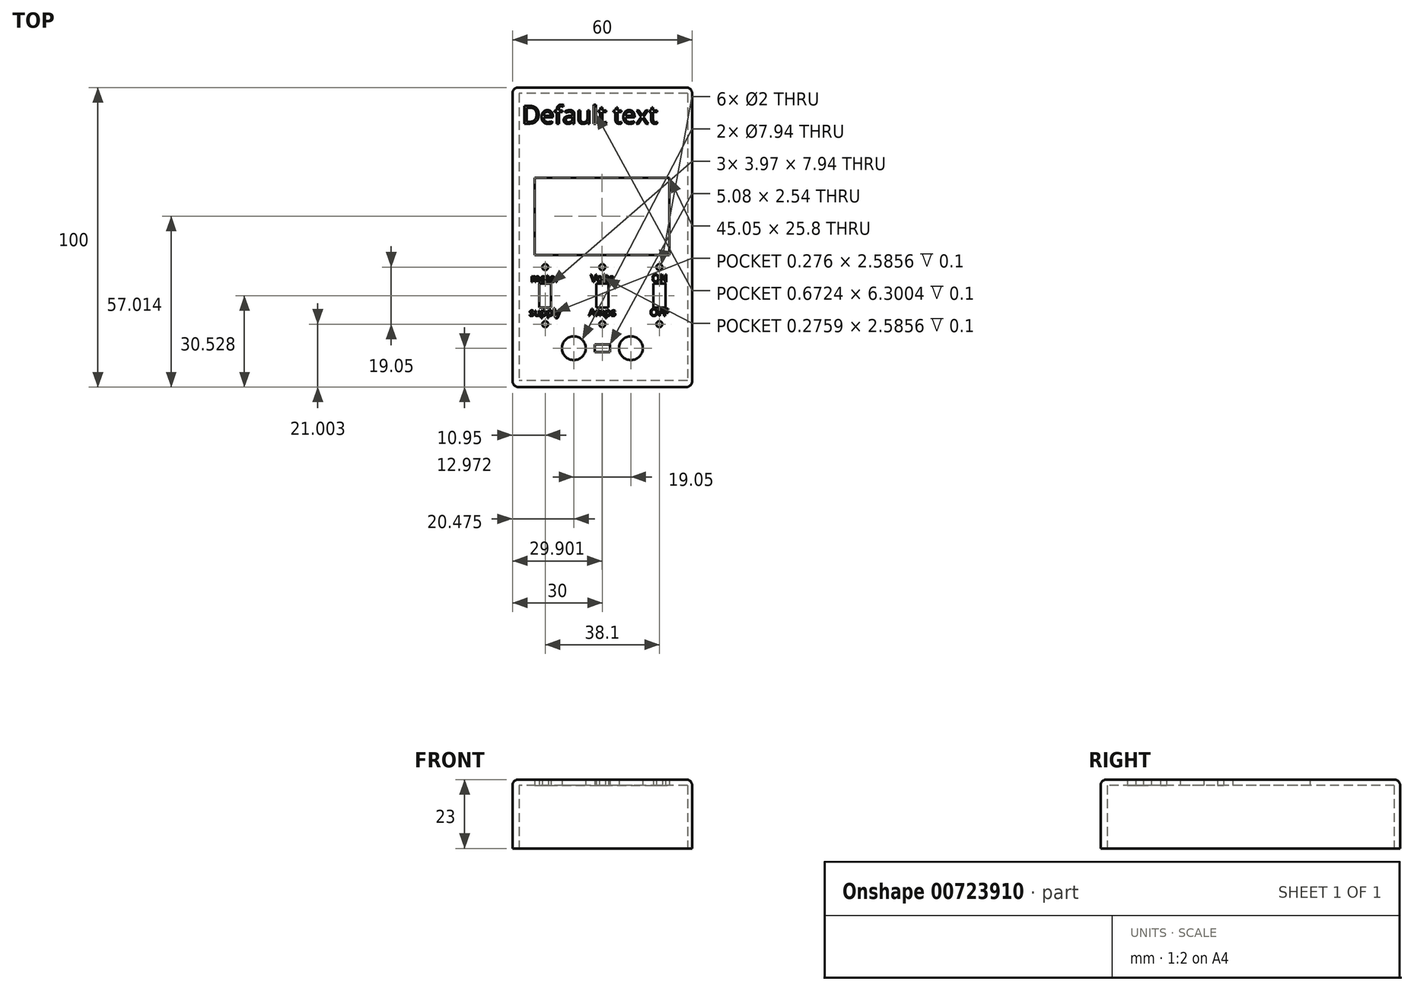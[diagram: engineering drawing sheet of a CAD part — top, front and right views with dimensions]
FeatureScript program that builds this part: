
annotation { "Feature Type Name" : "Feature", "Feature Type Description" : "" }
export const myFeature = defineFeature(function(context is Context, id is Id, definition is map)
    precondition{}
    {
        {
            var Q0;
            Q0=qCreatedBy(makeId("Top.planeOp"),FACE);
            var sketch = newSketch(context, id + "F0", { "sketchPlane" : qUnion([Q0])});
            skLineSegment(sketch, "E0.bottom", {"start": v(28.4, 48) * mm, "end": v(-27.8, 48) * mm});
            skLineSegment(sketch, "E0.top", {"start": v(28.4, -47.8) * mm, "end": v(-27.8, -47.8) * mm});
            skLineSegment(sketch, "E0.left", {"start": v(28.4, 48) * mm, "end": v(28.4, -47.8) * mm});
            skLineSegment(sketch, "E0.right", {"start": v(-27.8, 48) * mm, "end": v(-27.8, -47.8) * mm});
            skPoint(sketch, "E0.middle", {"position": v(0, 0) * mm});
            skLineSegment(sketch, "E1.bottom", {"start": v(23.81, 21.3) * mm, "end": v(-23.81, 21.3) * mm});
            skLineSegment(sketch, "E1.top", {"start": v(23.81, -7.27) * mm, "end": v(-23.81, -7.27) * mm});
            skLineSegment(sketch, "E1.left", {"start": v(23.81, 21.3) * mm, "end": v(23.81, -7.27) * mm});
            skLineSegment(sketch, "E1.right", {"start": v(-23.81, 21.3) * mm, "end": v(-23.81, -7.27) * mm});
            skPoint(sketch, "E1.middle", {"position": v(0, 7.01) * mm});
            skLineSegment(sketch, "E2.0", {"start": v(22.42, -5.88) * mm, "end": v(-22.62, -5.88) * mm});
            skLineSegment(sketch, "E2.1", {"start": v(22.42, 19.91) * mm, "end": v(22.42, -5.88) * mm});
            skLineSegment(sketch, "E2.2", {"start": v(22.42, 19.91) * mm, "end": v(-22.62, 19.91) * mm});
            skLineSegment(sketch, "E3", {"start": v(-22.62, 19.91) * mm, "end": v(-22.62, -5.88) * mm});
            skCircle(sketch, "E4", {"center": v(-9.52, -37.03) * mm, "radius": 3.97 * mm});
            skCircle(sketch, "E5", {"center": v(9.52, -37.03) * mm, "radius": 3.97 * mm});
            skCircle(sketch, "E6", {"center": v(9.52, -37.03) * mm, "radius": 5.56 * mm});
            skCircle(sketch, "E7", {"center": v(-9.52, -37.03) * mm, "radius": 5.56 * mm});
            skLineSegment(sketch, "E8", {"start": v(-9.52, -37.03) * mm, "end": v(9.52, -37.03) * mm, "construction": true});
            skPoint(sketch, "E9", {"position": v(0, -37.03) * mm});
            skLineSegment(sketch, "E10.bottom", {"start": v(2.54, -35.76) * mm, "end": v(-2.54, -35.76) * mm});
            skLineSegment(sketch, "E10.top", {"start": v(2.54, -38.3) * mm, "end": v(-2.54, -38.3) * mm});
            skLineSegment(sketch, "E10.left", {"start": v(2.54, -35.76) * mm, "end": v(2.54, -38.3) * mm});
            skLineSegment(sketch, "E10.right", {"start": v(-2.54, -35.76) * mm, "end": v(-2.54, -38.3) * mm});
            skLineSegment(sketch, "E11.bottom", {"start": v(30, 50) * mm, "end": v(-30, 50) * mm});
            skLineSegment(sketch, "E11.top", {"start": v(30, -50) * mm, "end": v(-30, -50) * mm});
            skLineSegment(sketch, "E11.left", {"start": v(30, 50) * mm, "end": v(30, -50) * mm});
            skLineSegment(sketch, "E11.right", {"start": v(-30, 50) * mm, "end": v(-30, -50) * mm});
            skLineSegment(sketch, "E12.bottom", {"start": v(-11.5, 21.5) * mm, "end": v(11.31, 21.5) * mm, "construction": true});
            skLineSegment(sketch, "E12.top", {"start": v(-11.5, -7.47) * mm, "end": v(11.31, -7.47) * mm, "construction": true});
            skLineSegment(sketch, "E12.left", {"start": v(-11.5, 21.5) * mm, "end": v(-11.5, -7.47) * mm, "construction": true});
            skLineSegment(sketch, "E12.right", {"start": v(11.31, 21.5) * mm, "end": v(11.31, -7.47) * mm, "construction": true});
            skLineSegment(sketch, "E13.bottom", {"start": v(-24.8, 48) * mm, "end": v(23.7, 48) * mm});
            skLineSegment(sketch, "E13.top", {"start": v(-24.8, 21.5) * mm, "end": v(23.7, 21.5) * mm});
            skLineSegment(sketch, "E13.left", {"start": v(-24.8, 48) * mm, "end": v(-24.8, 21.5) * mm});
            skLineSegment(sketch, "E13.right", {"start": v(23.7, 48) * mm, "end": v(23.7, 21.5) * mm});
            skLineSegment(sketch, "E14.bottom", {"start": v(1.98, -15.5) * mm, "end": v(-1.98, -15.5) * mm});
            skLineSegment(sketch, "E14.top", {"start": v(1.98, -23.44) * mm, "end": v(-1.98, -23.44) * mm});
            skLineSegment(sketch, "E14.left", {"start": v(1.98, -15.5) * mm, "end": v(1.98, -23.44) * mm});
            skLineSegment(sketch, "E14.right", {"start": v(-1.98, -15.5) * mm, "end": v(-1.98, -23.44) * mm});
            skPoint(sketch, "E14.middle", {"position": v(0, -19.47) * mm});
            skLineSegment(sketch, "E15.bottom", {"start": v(3.97, -7.47) * mm, "end": v(-3.97, -7.47) * mm});
            skLineSegment(sketch, "E15.top", {"start": v(3.97, -31.47) * mm, "end": v(-3.97, -31.47) * mm});
            skLineSegment(sketch, "E15.left", {"start": v(3.97, -7.47) * mm, "end": v(3.97, -31.47) * mm});
            skLineSegment(sketch, "E15.right", {"start": v(-3.97, -7.47) * mm, "end": v(-3.97, -31.47) * mm});
            skLineSegment(sketch, "E16", {"start": v(0, -29) * mm, "end": v(0, -9.95) * mm, "construction": true});
            skCircle(sketch, "E17", {"center": v(0, -29) * mm, "radius": 1 * mm});
            skCircle(sketch, "E18", {"center": v(0, -9.95) * mm, "radius": 1 * mm});
            skLineSegment(sketch, "E19.direction1", {"start": v(-3.97, -31.47) * mm, "end": v(15.08, -31.47) * mm, "construction": true});
            skCircle(sketch, "E20.0.1.0", {"center": v(19.05, -29) * mm, "radius": 1 * mm});
            skLineSegment(sketch, "E20.2.1.0", {"start": v(21.03, -15.5) * mm, "end": v(21.03, -23.44) * mm});
            skLineSegment(sketch, "E20.5.1.0", {"start": v(23.02, -7.47) * mm, "end": v(23.02, -31.47) * mm});
            skLineSegment(sketch, "E20.8.1.0", {"start": v(23.02, -31.47) * mm, "end": v(15.08, -31.47) * mm});
            skLineSegment(sketch, "E20.11.1.0", {"start": v(21.03, -23.44) * mm, "end": v(17.07, -23.44) * mm});
            skLineSegment(sketch, "E20.14.1.0", {"start": v(21.03, -15.5) * mm, "end": v(17.07, -15.5) * mm});
            skLineSegment(sketch, "E20.17.1.0", {"start": v(23.02, -7.47) * mm, "end": v(15.08, -7.47) * mm});
            skCircle(sketch, "E20.20.1.0", {"center": v(19.05, -9.95) * mm, "radius": 1 * mm});
            skLineSegment(sketch, "E20.22.1.0", {"start": v(17.07, -15.5) * mm, "end": v(17.07, -23.44) * mm});
            skLineSegment(sketch, "E20.25.1.0", {"start": v(15.08, -7.47) * mm, "end": v(15.08, -31.47) * mm});
            skCircle(sketch, "E21.1.0.0", {"center": v(-19.05, -29) * mm, "radius": 1 * mm});
            skLineSegment(sketch, "E21.1.0.1", {"start": v(-17.07, -15.5) * mm, "end": v(-17.07, -23.44) * mm});
            skLineSegment(sketch, "E21.1.0.2", {"start": v(-15.08, -7.47) * mm, "end": v(-15.08, -31.47) * mm});
            skLineSegment(sketch, "E21.1.0.3", {"start": v(-17.07, -23.44) * mm, "end": v(-21.03, -23.44) * mm});
            skLineSegment(sketch, "E21.1.0.4", {"start": v(-17.07, -15.5) * mm, "end": v(-21.03, -15.5) * mm});
            skLineSegment(sketch, "E21.1.0.5", {"start": v(-15.08, -7.47) * mm, "end": v(-23.02, -7.47) * mm});
            skLineSegment(sketch, "E21.1.0.6", {"start": v(-21.03, -15.5) * mm, "end": v(-21.03, -23.44) * mm});
            skCircle(sketch, "E21.1.0.7", {"center": v(-19.05, -9.95) * mm, "radius": 1 * mm});
            skLineSegment(sketch, "E21.1.0.8", {"start": v(-23.02, -7.47) * mm, "end": v(-23.02, -31.47) * mm});
            skLineSegment(sketch, "E21.direction1", {"start": v(-3.97, -31.47) * mm, "end": v(-23.02, -31.47) * mm, "construction": true});
            skLineSegment(sketch, "E22", {"start": v(-23.02, -31.47) * mm, "end": v(-15.08, -31.47) * mm});
            skSolve(sketch);
        }
        {
            var Q0;
            Q0=qCreatedBy(makeId("Top.planeOp"),FACE);
            var sketch = newSketch(context, id + "F1", { "sketchPlane" : qUnion([Q0])});
            skLineSegment(sketch, "E23.0.0", {"start": v(22.42, 19.91) * mm, "end": v(-22.62, 19.91) * mm});
            skLineSegment(sketch, "E23.0.1", {"start": v(-22.62, 19.91) * mm, "end": v(-22.62, -5.88) * mm});
            skLineSegment(sketch, "E23.0.2", {"start": v(-22.62, -5.88) * mm, "end": v(22.42, -5.88) * mm});
            skLineSegment(sketch, "E23.0.3", {"start": v(22.42, -5.88) * mm, "end": v(22.42, 19.91) * mm});
            skLineSegment(sketch, "E24.0", {"start": v(1.98, -15.5) * mm, "end": v(-1.98, -15.5) * mm});
            skLineSegment(sketch, "E25.0", {"start": v(-1.98, -15.5) * mm, "end": v(-1.98, -23.44) * mm});
            skLineSegment(sketch, "E26.0", {"start": v(1.98, -23.44) * mm, "end": v(-1.98, -23.44) * mm});
            skLineSegment(sketch, "E27.0", {"start": v(1.98, -15.5) * mm, "end": v(1.98, -23.44) * mm});
            skCircle(sketch, "E28.0", {"center": v(0, -29) * mm, "radius": 1 * mm});
            skCircle(sketch, "E29.0", {"center": v(0, -9.95) * mm, "radius": 1 * mm});
            skCircle(sketch, "E30.0", {"center": v(9.52, -37.03) * mm, "radius": 3.97 * mm});
            skLineSegment(sketch, "E31.0", {"start": v(2.54, -35.76) * mm, "end": v(-2.54, -35.76) * mm});
            skLineSegment(sketch, "E32.0", {"start": v(2.54, -38.3) * mm, "end": v(-2.54, -38.3) * mm});
            skLineSegment(sketch, "E33.0", {"start": v(2.54, -35.76) * mm, "end": v(2.54, -38.3) * mm});
            skLineSegment(sketch, "E34.0", {"start": v(-2.54, -35.76) * mm, "end": v(-2.54, -38.3) * mm});
            skCircle(sketch, "E35.0", {"center": v(-9.52, -37.03) * mm, "radius": 3.97 * mm});
            skLineSegment(sketch, "E36.0", {"start": v(30, 50) * mm, "end": v(-30, 50) * mm, "construction": true});
            skLineSegment(sketch, "E37.0", {"start": v(-30, 50) * mm, "end": v(-30, -50) * mm, "construction": true});
            skLineSegment(sketch, "E38.0", {"start": v(30, -50) * mm, "end": v(-30, -50) * mm, "construction": true});
            skLineSegment(sketch, "E39.0", {"start": v(30, 50) * mm, "end": v(30, -50) * mm, "construction": true});
            skLineSegment(sketch, "E40.0.0", {"start": v(21.03, -15.5) * mm, "end": v(17.07, -15.5) * mm});
            skLineSegment(sketch, "E40.0.1", {"start": v(17.07, -15.5) * mm, "end": v(17.07, -23.44) * mm});
            skLineSegment(sketch, "E40.0.2", {"start": v(17.07, -23.44) * mm, "end": v(21.03, -23.44) * mm});
            skLineSegment(sketch, "E40.0.3", {"start": v(21.03, -23.44) * mm, "end": v(21.03, -15.5) * mm});
            skLineSegment(sketch, "E41.0.0", {"start": v(-17.07, -15.5) * mm, "end": v(-21.03, -15.5) * mm});
            skLineSegment(sketch, "E41.0.1", {"start": v(-21.03, -15.5) * mm, "end": v(-21.03, -23.44) * mm});
            skLineSegment(sketch, "E41.0.2", {"start": v(-21.03, -23.44) * mm, "end": v(-17.07, -23.44) * mm});
            skLineSegment(sketch, "E41.0.3", {"start": v(-17.07, -23.44) * mm, "end": v(-17.07, -15.5) * mm});
            skCircle(sketch, "E42.0.0", {"center": v(-19.05, -9.95) * mm, "radius": 1 * mm});
            skCircle(sketch, "E43.0.0", {"center": v(-19.05, -29) * mm, "radius": 1 * mm});
            skCircle(sketch, "E44.0.0", {"center": v(19.05, -29) * mm, "radius": 1 * mm});
            skCircle(sketch, "E45.0.0", {"center": v(19.05, -9.95) * mm, "radius": 1 * mm});
            skSolve(sketch);
        }
        {
            var Q0;
            Q0=qCreatedBy(makeId("Top.planeOp"),FACE);
            var sketch = newSketch(context, id + "F2", { "sketchPlane" : qUnion([Q0])});
            skLineSegment(sketch, "E46.0", {"start": v(30, 50) * mm, "end": v(-30, 50) * mm});
            skLineSegment(sketch, "E47.0", {"start": v(28.4, 48) * mm, "end": v(-27.8, 48) * mm});
            skLineSegment(sketch, "E48.0", {"start": v(-27.8, 48) * mm, "end": v(-27.8, -47.8) * mm});
            skLineSegment(sketch, "E49.0", {"start": v(-30, 50) * mm, "end": v(-30, -50) * mm});
            skLineSegment(sketch, "E50.0", {"start": v(28.4, 48) * mm, "end": v(28.4, -47.8) * mm});
            skLineSegment(sketch, "E51.0", {"start": v(28.4, -47.8) * mm, "end": v(-27.8, -47.8) * mm});
            skLineSegment(sketch, "E52.0", {"start": v(30, -50) * mm, "end": v(-30, -50) * mm});
            skLineSegment(sketch, "E53.0", {"start": v(30, 50) * mm, "end": v(30, -50) * mm});
            skSolve(sketch);
        }
        {
            var Q0;
            Q0=makeQuery(id+"F2.imprint","IMPRINT",FACE,{"disambiguationData":[TD([[makeQuery(id+"F2.imprint","IMPRINT",EDGE,{"derivedFrom":sQuery(id+"F2.wireOp",EDGE,"E46.0")}),1.0]])]});
            var Q1;
            Q1=makeQuery(id+"F2.imprint","IMPRINT",FACE,{"disambiguationData":[TD([[makeQuery(id+"F2.imprint","IMPRINT",EDGE,{"derivedFrom":sQuery(id+"F2.wireOp",EDGE,"E47.0")}),1.0]])]});
            extrude(context, id + "F3", {"entities" : qUnion([Q0, Q1]), "depth" : 23 * mm, "offsetDistance" : 25.4 * mm});
        }
        {
            var Q0;
            Q0=makeQuery(id+"F2.imprint","IMPRINT",FACE,{"disambiguationData":[TD([[makeQuery(id+"F2.imprint","IMPRINT",EDGE,{"derivedFrom":sQuery(id+"F2.wireOp",EDGE,"E47.0")}),1.0]])]});
            extrude(context, id + "F4", {"entities" : qUnion([Q0]), "operationType" : NewBodyOperationType.REMOVE, "depth" : 21 * mm, "offsetDistance" : 25.4 * mm});
        }
        {
            var Q0;
            Q0=makeQuery(id+"F3.opExtrude","CAP_EDGE",EDGE,{"disambiguationData":[OSD([sQuery(id+"F2.wireOp",EDGE,"E52.0")])],"isStart":false});
            var Q1;
            Q1=makeQuery(id+"F3.opExtrude","CAP_EDGE",EDGE,{"disambiguationData":[OSD([sQuery(id+"F2.wireOp",EDGE,"E53.0")])],"isStart":false});
            var Q2;
            Q2=makeQuery(id+"F3.opExtrude","CAP_EDGE",EDGE,{"disambiguationData":[OSD([sQuery(id+"F2.wireOp",EDGE,"E49.0")])],"isStart":false});
            var Q3;
            Q3=makeQuery(id+"F3.opExtrude","CAP_EDGE",EDGE,{"disambiguationData":[OSD([sQuery(id+"F2.wireOp",EDGE,"E46.0")])],"isStart":false});
            var Q4;
            Q4=makeQuery(id+"F3.opExtrude","SWEPT_EDGE",EDGE,{"disambiguationData":[OSD([sQuery(id+"F2.wireOp",EDGE,"E46.0"),sQuery(id+"F2.wireOp",EDGE,"E49.0")])]});
            var Q5;
            Q5=makeQuery(id+"F3.opExtrude","SWEPT_EDGE",EDGE,{"disambiguationData":[OSD([sQuery(id+"F2.wireOp",EDGE,"E49.0"),sQuery(id+"F2.wireOp",EDGE,"E52.0")])]});
            var Q6;
            Q6=makeQuery(id+"F3.opExtrude","SWEPT_EDGE",EDGE,{"disambiguationData":[OSD([sQuery(id+"F2.wireOp",EDGE,"E52.0"),sQuery(id+"F2.wireOp",EDGE,"E53.0")])]});
            var Q7;
            Q7=makeQuery(id+"F3.opExtrude","SWEPT_EDGE",EDGE,{"disambiguationData":[OSD([sQuery(id+"F2.wireOp",EDGE,"E46.0"),sQuery(id+"F2.wireOp",EDGE,"E53.0")])]});
            fillet(context, id + "F5", {"entities" : qUnion([Q0, Q1, Q2, Q3, Q4, Q5, Q6, Q7]), "radius" : 2 * mm, "tangentPropagation" : true, "allowEdgeOverflow" : false});
        }
        {
            var Q0;
            Q0=makeQuery(id+"F1.imprint","IMPRINT",FACE,{"disambiguationData":[TD([[makeQuery(id+"F1.imprint","IMPRINT",EDGE,{"derivedFrom":sQuery(id+"F1.wireOp",EDGE,"E23.0.0")}),1.0]])]});
            var Q1;
            Q1=makeQuery(id+"F1.imprint","IMPRINT",FACE,{"disambiguationData":[TD([[makeQuery(id+"F1.imprint","IMPRINT",EDGE,{"derivedFrom":sQuery(id+"F1.wireOp",EDGE,"E24.0")}),1.0]])]});
            var Q2;
            Q2=makeQuery(id+"F1.imprint","IMPRINT",FACE,{"disambiguationData":[TD([[makeQuery(id+"F1.imprint","IMPRINT",EDGE,{"derivedFrom":sQuery(id+"F1.wireOp",EDGE,"E29.0")}),1.0]])]});
            var Q3;
            Q3=makeQuery(id+"F1.imprint","IMPRINT",FACE,{"disambiguationData":[TD([[makeQuery(id+"F1.imprint","IMPRINT",EDGE,{"derivedFrom":sQuery(id+"F1.wireOp",EDGE,"E28.0")}),1.0]])]});
            var Q4;
            Q4=makeQuery(id+"F1.imprint","IMPRINT",FACE,{"disambiguationData":[TD([[makeQuery(id+"F1.imprint","IMPRINT",EDGE,{"derivedFrom":sQuery(id+"F1.wireOp",EDGE,"E35.0")}),1.0]])]});
            var Q5;
            Q5=makeQuery(id+"F1.imprint","IMPRINT",FACE,{"disambiguationData":[TD([[makeQuery(id+"F1.imprint","IMPRINT",EDGE,{"derivedFrom":sQuery(id+"F1.wireOp",EDGE,"E30.0")}),1.0]])]});
            var Q6;
            Q6=makeQuery(id+"F1.imprint","IMPRINT",FACE,{"disambiguationData":[TD([[makeQuery(id+"F1.imprint","IMPRINT",EDGE,{"derivedFrom":sQuery(id+"F1.wireOp",EDGE,"E31.0")}),1.0]])]});
            var Q7;
            Q7=makeQuery(id+"F1.imprint","IMPRINT",FACE,{"disambiguationData":[TD([[makeQuery(id+"F1.imprint","IMPRINT",EDGE,{"derivedFrom":sQuery(id+"F1.wireOp",EDGE,"E41.0.0")}),1.0]])]});
            var Q8;
            Q8=makeQuery(id+"F1.imprint","IMPRINT",FACE,{"disambiguationData":[TD([[makeQuery(id+"F1.imprint","IMPRINT",EDGE,{"derivedFrom":sQuery(id+"F1.wireOp",EDGE,"E43.0.0")}),1.0]])]});
            var Q9;
            Q9=makeQuery(id+"F1.imprint","IMPRINT",FACE,{"disambiguationData":[TD([[makeQuery(id+"F1.imprint","IMPRINT",EDGE,{"derivedFrom":sQuery(id+"F1.wireOp",EDGE,"E42.0.0")}),1.0]])]});
            var Q10;
            Q10=makeQuery(id+"F1.imprint","IMPRINT",FACE,{"disambiguationData":[TD([[makeQuery(id+"F1.imprint","IMPRINT",EDGE,{"derivedFrom":sQuery(id+"F1.wireOp",EDGE,"E45.0.0")}),1.0]])]});
            var Q11;
            Q11=makeQuery(id+"F1.imprint","IMPRINT",FACE,{"disambiguationData":[TD([[makeQuery(id+"F1.imprint","IMPRINT",EDGE,{"derivedFrom":sQuery(id+"F1.wireOp",EDGE,"E40.0.0")}),1.0]])]});
            var Q12;
            Q12=makeQuery(id+"F1.imprint","IMPRINT",FACE,{"disambiguationData":[TD([[makeQuery(id+"F1.imprint","IMPRINT",EDGE,{"derivedFrom":sQuery(id+"F1.wireOp",EDGE,"E44.0.0")}),1.0]])]});
            extrude(context, id + "F6", {"entities" : qUnion([Q0, Q1, Q2, Q3, Q4, Q5, Q6, Q7, Q8, Q9, Q10, Q11, Q12]), "operationType" : NewBodyOperationType.REMOVE, "endBound" : BoundingType.THROUGH_ALL, "depth" : 25.4 * mm, "offsetDistance" : 25.4 * mm});
        }
        {
            var Q0;
            Q0=makeQuery(id+"F3.opExtrude","CAP_FACE",FACE,{"disambiguationData":[OSD([sQuery(id+"F2.wireOp",EDGE,"E46.0"),sQuery(id+"F2.wireOp",EDGE,"E49.0"),sQuery(id+"F2.wireOp",EDGE,"E52.0"),sQuery(id+"F2.wireOp",EDGE,"E53.0")])],"isStart":false});
            var sketch = newSketch(context, id + "F7", { "sketchPlane" : qUnion([Q0])});
            skText(sketch, "E54", { "text": "Default text", "fontName": "OpenSans-Regular.ttf"});
            skText(sketch, "E55", { "text": "meter", "fontName": "OpenSans-Regular.ttf"});
            skText(sketch, "E56", { "text": "supply", "fontName": "OpenSans-Regular.ttf"});
            skPoint(sketch, "E57", {"position": v(-19.05, -15.5) * mm});
            skText(sketch, "E58", { "text": "Amps", "fontName": "OpenSans-Regular.ttf"});
            skText(sketch, "E59", { "text": "Volts", "fontName": "OpenSans-Regular.ttf"});
            skPoint(sketch, "E60", {"position": v(0, -15.5) * mm});
            skText(sketch, "E61", { "text": "ON", "fontName": "OpenSans-Regular.ttf"});
            skText(sketch, "E62", { "text": "OFF", "fontName": "OpenSans-Regular.ttf"});
            skPoint(sketch, "E63", {"position": v(19.05, -15.5) * mm});
            skPoint(sketch, "E64", {"position": v(19.05, -23.44) * mm});
            skPoint(sketch, "E65", {"position": v(0, -23.44) * mm});
            skPoint(sketch, "E66", {"position": v(-19.05, -23.44) * mm});
            const initialGuessF7  = {"E54": [-0.02678, 0.03794, 1, 0, 0.00597], "E55": [-0.02392, -0.01489, 1, 0, 0.00245], "E56": [-0.02438, -0.02625, 1, 0, 0.00245], "E58": [-0.00454, -0.02625, 1, 0, 0.00245], "E59": [-0.00391, -0.01489, 1, 0, 0.00245], "E61": [0.0165, -0.01489, 1, 0, 0.00245], "E62": [0.0159, -0.02625, 1, 0, 0.00245]};
            skSetInitialGuess(sketch, initialGuessF7);
            skSolve(sketch);
        }
        {
            var Q0;
            Q0 = qSketchRegion(id + "F7", true);
            extrude(context, id + "F8", {"entities" : qUnion([Q0]), "operationType" : NewBodyOperationType.REMOVE, "oppositeDirection" : true, "depth" : .1 * mm, "offsetDistance" : 25.4 * mm});
        }
    });
